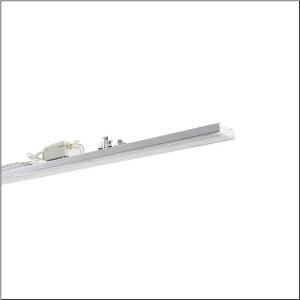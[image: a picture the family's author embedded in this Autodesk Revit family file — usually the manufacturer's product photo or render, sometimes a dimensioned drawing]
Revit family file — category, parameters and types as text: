
# Revit family: licross_11_recessed_mo_51tl14cn485g
name_source: partatom
category: Lighting Fixtures
units: mm (PartAtom-declared; Revit-internal decimal feet)

## family parameters
Cut with Voids When Loaded = No
Host = Face
Light Source = No
Part Type = Normal
Room Calculation Point = No
Round Connector Dimension = Use Diameter
Shared = No

## types (1)
- --- (1 x LED, 8570 lm, 49.3 W, 4000K)
    Apparent Load = 49 VA
    CIE Flux Codes = 56 84 97 100 100
    Color Rendering = 80
    Color Temperature = 4000K
    Default Elevation = 1800 mm
    Description = Licross 11 Recessed MO, luminaire insert, of sheet steel, coil coated, white, length: 1.500mm, width: 66mm, height: 67mm, LED rated luminous flux: 8.570lm, light colour: 840, SDCM (Standard Deviation of Colour Matching)MacAdam ≤ 2 SDCM (initial), control gear: ON/OFF Multilumen, CLOi, with plug, 3-pole, with phase selection, mains connection: 220..240V, AC, 50/60Hz, start of lifetime: 49W, end of service life: 55W, internal wiring halogen-free, primary light control with lens, of plastic, primary optical cover: cover, of PMMA, light emission: direct distribution, primary light characteristic: asymmetric, protection rating (complete): IP40, insulation class (complete): insulation class I (protective earthing), certification: CE, ENEC, VDE, UKCA, protection symbol: D if used in an environment without relevant dust loads with corresponding accessories, impact resistance: IK06, permissible ambient temperature for indoor applications: -35..+40°C, corresponds to IFS (International Featured Standards) requirements for safety and quality in the food industry, reducing of maximum allowable ambient temperature of 5°C with ceiling mounting, LABS conformity tested according to VDMA 24364:2018-05, The light source and the operating device comply with the requirements of the Ecodesign Regulation (EU) 2019/2020 and are replaceable in accordance with this regulation, packaging unit: 1 piece
    Height = 58 mm
    Lamp = 1 x LED
    Lamp Light Flux = 8570 lm
    Lamp Power = 49.3 W
    Lamp count = 1
    Length = 1500 mm
    Luminous efficacy = 174 lm/W
    Manufacturer = Siteco
    ModVariant = No
    Model = 51TL14CN485G
    Mounting Place = Ceiling
    Mounting Type = Pendant
    Number of Poles = 1
    OnlyDefault = Yes
    Power Factor = 1
    Product Name = Licross 11 Recessed MO
    Product group = luminaire insert | ceiling pendant
    ProductGroupID = 901
    Protection Class = Protection class I
    Protection Degree = IP 40
    RLX_Detail_Level = 1
    RLX_Emergency_Light_Flux = 0 lm
    RLX_Emergency_Type = 0
    RLX_Emergency_Type_DB = No
    RlxData = <blob elided: 23057 chars, md5=36f8e827>
    Socket = socket
    Standby Power = 0 W
    System Light Flux = 8570 lm
    System Power = 49 W
    Type Comments = factory setting: luminous flux: 100 % | (A | C | E) | 113 mA
    Type Image = l_1296930.jpg
    URL = http://relux.com
    VarID = @adj_000469
    Voltage = 0 V
    Weight = 0.00 kg
    Width = 66 mm

## geometry (parser evidence)
native form markers: Blend x4, Sweep x12
no freeform markers — native parametric forms only
